# Revit family: FA_КолодецЗаземления_88203_EZETEK
name_source: partatom
category: Системы пожарной сигнализации
revit_build: Autodesk Revit 2017 (Build: 20170118_1100(x64)
units: mm (PartAtom-declared; Revit-internal decimal feet)

## family parameters
Всегда вертикально = Да
На основе рабочей плоскости = Нет
Общий = Да
При загрузке вырезать с полостями = Нет
Размер круглого соединителя = Использовать радиус
Сохранять ориентацию аннотаций = Нет
Тип детали = Нормальный
Точка расчета площади = Нет

## types (1)
- КолодецЗаземления_88203_EZETEK
    ADSK_Версия Revit = 2017
    ADSK_Единица измерения = шт.
    ADSK_Завод-изготовитель = Ezetek
    ADSK_Код изделия = 88203
    ADSK_Количество = 1
    ADSK_Марка = 88203
    ADSK_Масса = 0.91
    ADSK_Масса_Текст = 0.91
    ADSK_Материал = BIMLIB_Пластик_Черный_EZETEK
    ADSK_Наименование = Колодец заземления контрольно-измерительный 200х200х200 мм, пластик
    ADSK_Обозначение = 88203
    URL = https://ezetek.ru
    Группа модели = Электролитическое заземление
    Изготовитель = Ezetek
    Описание = Колодец заземления изготовлен из пластмассы, позволяет осуществлять осмотр соединения «заземлитель — заземляющий проводник», а также проводить контрольные измерения сопротивления системы заземления. Колодец заземления монтируется в грунт на одном уровне с поверхностью земли. Размер 200 х 200 х 200 мм, максимально допустимая нагрузка 12 кг/см 2.
    Угол = 90.00°
